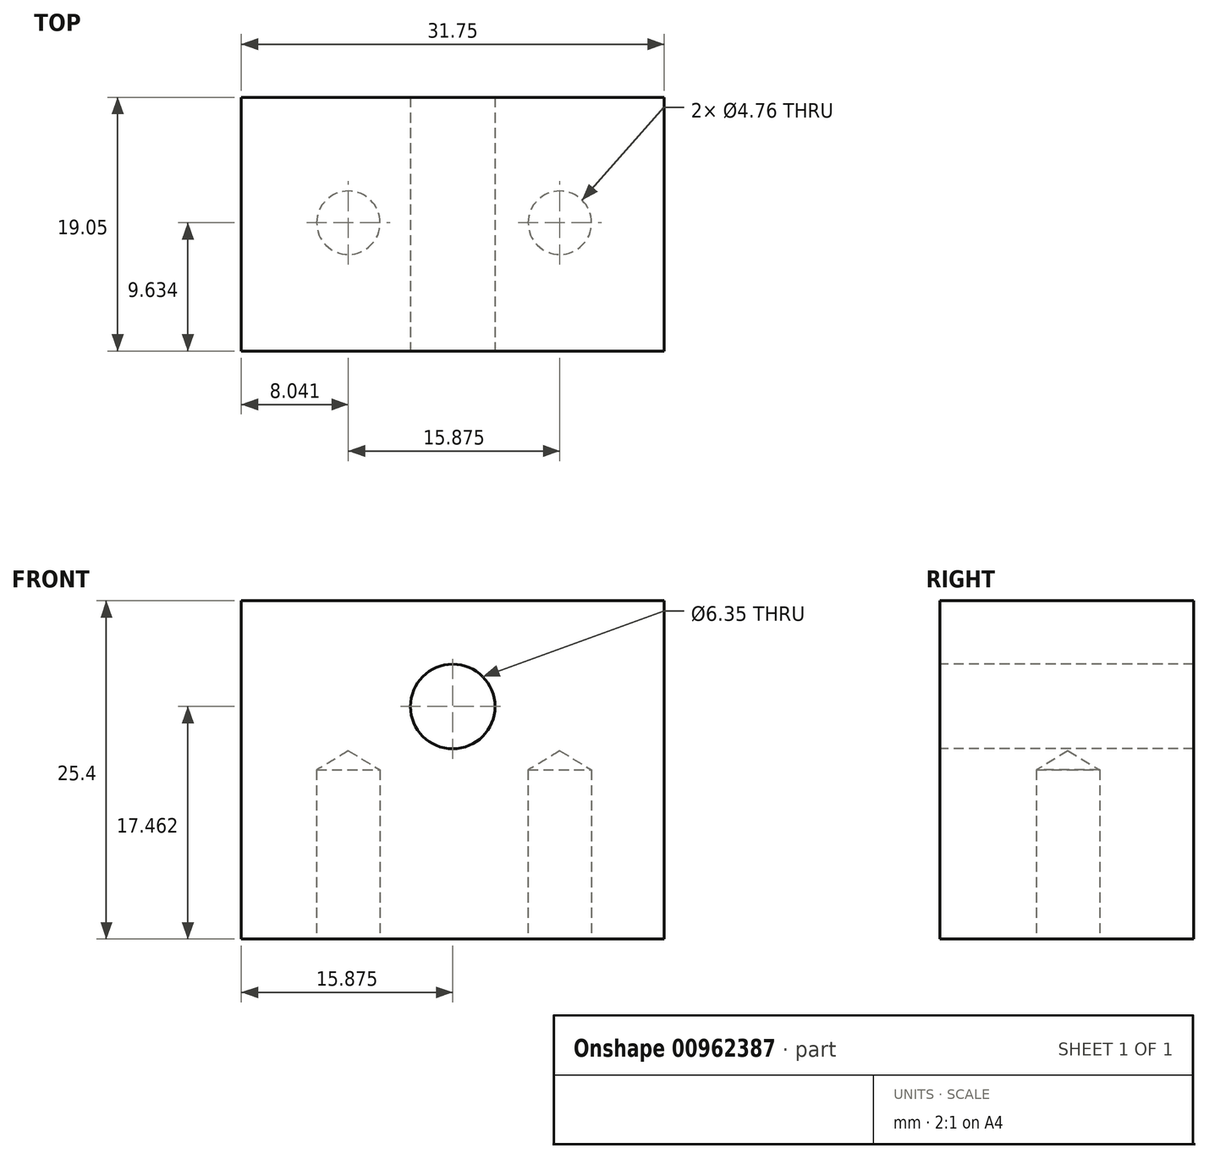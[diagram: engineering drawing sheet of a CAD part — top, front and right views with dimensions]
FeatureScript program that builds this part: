
annotation { "Feature Type Name" : "Feature", "Feature Type Description" : "" }
export const myFeature = defineFeature(function(context is Context, id is Id, definition is map)
    precondition{}
    {
        {
            var Q0;
            Q0=qCreatedBy(makeId("Top.planeOp"),FACE);
            var sketch = newSketch(context, id + "F0", { "sketchPlane" : qUnion([Q0])});
            skLineSegment(sketch, "E0.bottom", {"start": v(0, 0) * mm, "end": v(31.75, 0) * mm});
            skLineSegment(sketch, "E0.top", {"start": v(0, 19.05) * mm, "end": v(31.75, 19.05) * mm});
            skLineSegment(sketch, "E0.left", {"start": v(0, 0) * mm, "end": v(0, 19.05) * mm});
            skLineSegment(sketch, "E0.right", {"start": v(31.75, 0) * mm, "end": v(31.75, 19.05) * mm});
            skSolve(sketch);
        }
        {
            var Q0;
            Q0=qSketchRegion(id+"F0",true);
            extrude(context, id + "F1", {"entities" : qUnion([Q0]), "depth" : 25.4 * mm, "offsetDistance" : 25.4 * mm});
        }
        {
            var Q0;
            Q0=makeQuery(id+"F0.imprint","IMPRINT",FACE,{"disambiguationData":[TD([[makeQuery(id+"F0.imprint","IMPRINT",EDGE,{"derivedFrom":sQuery(id+"F0.wireOp",EDGE,"E0.bottom")}),1.0]])]});
            var sketch = newSketch(context, id + "F2", { "sketchPlane" : qUnion([Q0])});
            skLineSegment(sketch, "E1.bottom", {"start": v(0.1, 0.1) * mm, "end": v(31.85, 0.1) * mm});
            skLineSegment(sketch, "E1.top", {"start": v(0.1, 19.16) * mm, "end": v(31.85, 19.16) * mm});
            skLineSegment(sketch, "E1.left", {"start": v(0.1, 0.1) * mm, "end": v(0.1, 19.16) * mm});
            skLineSegment(sketch, "E1.right", {"start": v(31.85, 0.1) * mm, "end": v(31.85, 19.16) * mm});
            skCircle(sketch, "E2", {"center": v(8.04, 9.63) * mm, "radius": 2.38 * mm});
            skCircle(sketch, "E3", {"center": v(23.92, 9.63) * mm, "radius": 2.38 * mm});
            skSolve(sketch);
        }
        {
            var Q0;
            Q0=sQuery(id+"F2.wireOp",VERTEX,"E2.center");
            var Q1;
            Q1=sQuery(id+"F2.wireOp",VERTEX,"E3.center");
            var Q2;
            Q2=makeQuery(id+"F1.opExtrude","SWEPT_BODY",BODY,{"disambiguationData":[OSD([sQuery(id+"F0.wireOp",EDGE,"E0.bottom"),sQuery(id+"F0.wireOp",EDGE,"E0.top"),sQuery(id+"F0.wireOp",EDGE,"E0.left"),sQuery(id+"F0.wireOp",EDGE,"E0.right")])]});
            hole(context, id + "F3", {"style" : HoleStyle.SIMPLE, "endStyle" : HoleEndStyle.BLIND, "oppositeDirection" : true, "holeDiameter" : 4.76 * mm, "majorDiameter" : 6.35 * mm, "holeDepth" : 12.7 * mm, "isTappedThrough" : true, "tappedDepth" : 12.7 * mm, "tapClearance" : 3, "startFromSketch" : true, "locations" : qUnion([Q0, Q1]), "scope" : qUnion([Q2])});
        }
        {
            var Q0;
            Q0=makeQuery(id+"F1.opExtrude","SWEPT_FACE",FACE,{"disambiguationData":[OSD([sQuery(id+"F0.wireOp",EDGE,"E0.bottom")])]});
            var sketch = newSketch(context, id + "F4", { "sketchPlane" : qUnion([Q0])});
            skCircle(sketch, "E4", {"center": v(15.88, 17.46) * mm, "radius": 3.18 * mm});
            skSolve(sketch);
        }
        {
            var Q0;
            Q0=sQuery(id+"F4.wireOp",VERTEX,"E4.center");
            var Q1;
            Q1=makeQuery(id+"F1.opExtrude","SWEPT_BODY",BODY,{"disambiguationData":[OSD([sQuery(id+"F0.wireOp",EDGE,"E0.bottom"),sQuery(id+"F0.wireOp",EDGE,"E0.top"),sQuery(id+"F0.wireOp",EDGE,"E0.left"),sQuery(id+"F0.wireOp",EDGE,"E0.right")])]});
            hole(context, id + "F5", {"style" : HoleStyle.SIMPLE, "endStyle" : HoleEndStyle.THROUGH, "holeDiameter" : 6.35 * mm, "majorDiameter" : 6.35 * mm, "isTappedThrough" : true, "tappedDepth" : 12.7 * mm, "tapClearance" : 3, "startFromSketch" : true, "locations" : qUnion([Q0]), "scope" : qUnion([Q1])});
        }
    });
